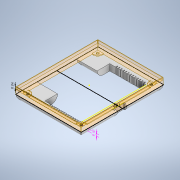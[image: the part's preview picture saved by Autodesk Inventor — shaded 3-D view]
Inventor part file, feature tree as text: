
AUTODESK INVENTOR PART (.ipt)
format: ipt  version: 2020 (Build 240168000, 168)  size: 1,344,512 bytes
history: native  units: mm
features: other x9, sketch x6, fillet x5, extrude x4, chamfer x1
ambient origin geometry x8: Origin, YZ Plane, XZ Plane, XY Plane, X Axis, Y Axis, Z Axis, Center Point
bodies: Body1 (feature_tree), Body2 (feature_tree), Body3 (feature_tree)
feature tree (25):
  other  "Casing_LCD_lip.ipt"
  other  "Annotations"
  extrude  "Extrusion5"  Depth=10.0mm
  chamfer  "Chamfer2"  Distance=3.0mm
  fillet  "Fillet7"  Radius=3.0mm
  fillet  "Fillet8"  Radius=3.0mm
  fillet  "Fillet9"  Radius=3.0mm
  fillet  "Fillet10"  Radius=3.0mm
  fillet  "Fillet11"  Radius=3.0mm
  extrude  "Extrusion7"  Depth=3.0mm
  sketch  "Sketch6"  dims[d24=3.0mm]
  extrude  "Extrusion8"  Depth=3.0mm
  extrude  "Extrusion9"  Depth=3.0mm
  other  "TaggingFeature1"
  sketch  "Sketch1"  dims[d0=10.0mm d19=55.0mm]
  other  "Srf2"
  sketch  "Sketch2"  dims[d20=55.0mm]
  sketch  "Sketch5"  dims[d23=9.7mm]
  sketch  "Sketch7"  dims[d25=3.0mm]
  sketch  "Sketch11"  dims[d26=3.0mm d27=3.0mm d28=3.0mm d29=3.0mm d30=3.0mm d31=3.0mm d32=3.0mm d33=3.0mm d34=7.05mm d35=7.05mm d36=7.05mm d37=7.05mm d38=7.05mm d39=7.05mm d40=7.05mm d41=7.05mm d42=7.05mm d43=3.0mm d44=3.0mm d45=3.0mm d46=7.05mm d47=7.05mm d48=7.05mm d49=354.6mm d50=177.3mm d52=10.0mm d53=0.0mm d57=30.0mm d75=17.0mm d76=2.0mm d77=45.0deg d82=28.0mm d83=4.0mm d84=1.0mm d85=4.0mm d89=2.0mm d90=10.0mm d93=10.0mm d94=50.0mm d95=40.0mm d96=20.0mm d97=25.0mm d99=27.4mm d100=0.0mm d101=10.0mm d102=282.0mm d103=141.0mm d123=10.0mm d124=5.0mm d125=0.0mm d126=0.0mm d129=10.0mm d130=16.0mm d131=16.0mm d132=16.0mm d133=16.0mm d134=3.0mm d135=0.0mm d136=1.0mm d137=1.0mm d78=1.696472mm d79=1.810348mm d80=9.1mm d86=5.107216mm d87=5.621346mm d88=9.043146mm d54=0.5mm d55=0.872665mm]
  other  "Solid1::Casing_LCD_lip.ipt"
  other  "Srf1"
  other  "Srf1::Derived"
  other  "Linear Dimension 1"
  other  "Linear Dimension 2"
